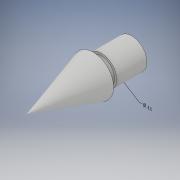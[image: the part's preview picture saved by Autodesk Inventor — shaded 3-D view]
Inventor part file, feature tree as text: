
AUTODESK INVENTOR PART (.ipt)
format: ipt  version: 2018 (Build 220112000, 112)  size: 130,560 bytes
history: native  units: in
note: dims shown in document units (in); Inventor stores cm internally (conversion verified against a paired STEP export)
features: other x2, revolve x1, sketch x1
ambient origin geometry x8: Origin, YZ Plane, XZ Plane, XY Plane, X Axis, Y Axis, Z Axis, Center Point
bodies: Solid1 (feature_tree)
feature tree (4):
  other  "Annotations"
  revolve  "Revolution1"  [1 undecoded]
  sketch  "Sketch1"  dims[d0=0.33in d1=0.04in d2=0.15in d3=0.1in d4=0.065in d5=0.075in d6=0.04in d7=0.01in d8=90.0deg d10=0.1811in d11=0.1528in d12=0.11in d9=2.1181in]
  other  "Diameter Dimension 1"
note: 1 required parameter value undecoded (feature->parameter linkage not recoverable at this tier; creation-order binding heuristic only, values carry confidence <= 0.55)
